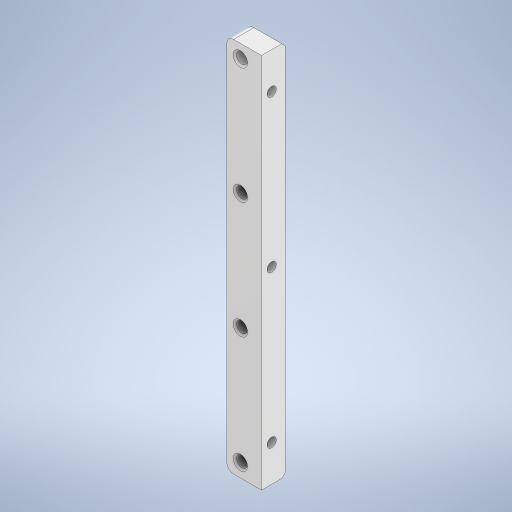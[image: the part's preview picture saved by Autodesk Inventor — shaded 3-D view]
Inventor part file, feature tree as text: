
AUTODESK INVENTOR PART (.ipt)
format: ipt  version: 2024 (Build 280153000, 153)  size: 283,648 bytes
history: native  units: mm
features: sketch x2, chamfer x2, hole x2, extrude x1, fillet x1
ambient origin geometry x8: Origin, YZ Plane, XZ Plane, XY Plane, X Axis, Y Axis, Z Axis, Center Point
bodies: Solid1 (feature_tree)
feature tree (8):
  sketch  "Sketch1"  dims[d0=20.5mm d2=40.0mm d4=69.0mm d5=10.0mm d7=10.0mm d9=8.0mm]
  extrude  "Extrusion1"  Depth=10.0mm
  fillet  "Fillet1"  Radius=8.0mm
  chamfer  "Chamfer1"  Distance=14.0mm
  hole  "Hole1"  [1 undecoded]
  hole  "Hole2"  [1 undecoded]
  chamfer  "Chamfer2"  Distance=180.0mm
  sketch  "Sketch2"  dims[d10=8.0mm d11=14.0mm d12=0.0mm d13=4.0mm d14=2.0mm d15=2.0mm d16=45.0deg d17=6.5mm d18=10.0mm d19=6.5mm d20=11.0mm d21=90.0deg d22=8.0mm d23=20.594885mm d24=180.0mm d25=6.0mm d26=5.4mm d27=6.0mm d28=9.5mm d29=6.5mm d30=90.0deg d31=8.0mm d32=20.594885mm d33=1.0mm d34=2.0mm d35=45.0deg]
note: 2 required parameter values undecoded (feature->parameter linkage not recoverable at this tier; creation-order binding heuristic only, values carry confidence <= 0.55)
